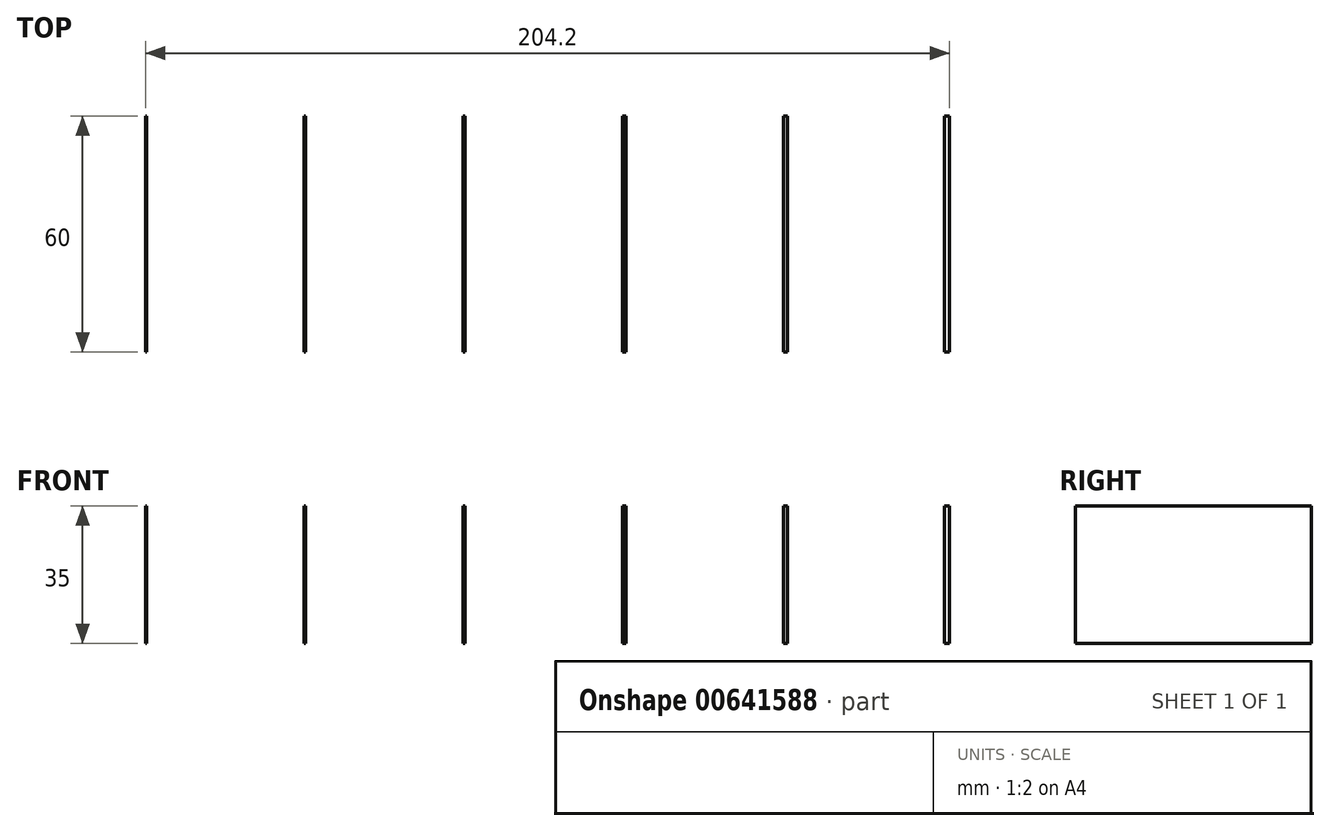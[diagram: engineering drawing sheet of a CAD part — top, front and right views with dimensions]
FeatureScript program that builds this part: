
annotation { "Feature Type Name" : "Feature", "Feature Type Description" : "" }
export const myFeature = defineFeature(function(context is Context, id is Id, definition is map)
    precondition{}
    {
        {
            var Q0;
            Q0=qCreatedBy(makeId("Top.planeOp"),FACE);
            var sketch = newSketch(context, id + "F0", { "sketchPlane" : qUnion([Q0])});
            skLineSegment(sketch, "E0.bottom", {"start": v(-7.2, 180) * mm, "end": v(-6, 180) * mm});
            skLineSegment(sketch, "E0.top", {"start": v(-7.2, 120) * mm, "end": v(-6, 120) * mm});
            skLineSegment(sketch, "E0.left", {"start": v(-7.2, 180) * mm, "end": v(-7.2, 120) * mm});
            skLineSegment(sketch, "E0.right", {"start": v(-6, 180) * mm, "end": v(-6, 120) * mm});
            skLineSegment(sketch, "E1.bottom", {"start": v(-47.2, 120) * mm, "end": v(-48.2, 120) * mm});
            skLineSegment(sketch, "E1.top", {"start": v(-47.2, 180) * mm, "end": v(-48.2, 180) * mm});
            skLineSegment(sketch, "E1.left", {"start": v(-47.2, 120) * mm, "end": v(-47.2, 180) * mm});
            skLineSegment(sketch, "E1.right", {"start": v(-48.2, 120) * mm, "end": v(-48.2, 180) * mm});
            skLineSegment(sketch, "E2.bottom", {"start": v(-88.2, 120) * mm, "end": v(-89, 120) * mm});
            skLineSegment(sketch, "E2.top", {"start": v(-88.2, 180) * mm, "end": v(-89, 180) * mm});
            skLineSegment(sketch, "E2.left", {"start": v(-88.2, 120) * mm, "end": v(-88.2, 180) * mm});
            skLineSegment(sketch, "E2.right", {"start": v(-89, 120) * mm, "end": v(-89, 180) * mm});
            skLineSegment(sketch, "E3.bottom", {"start": v(-129, 120) * mm, "end": v(-129.6, 120) * mm});
            skLineSegment(sketch, "E3.top", {"start": v(-129, 180) * mm, "end": v(-129.6, 180) * mm});
            skLineSegment(sketch, "E3.left", {"start": v(-129, 120) * mm, "end": v(-129, 180) * mm});
            skLineSegment(sketch, "E3.right", {"start": v(-129.6, 120) * mm, "end": v(-129.6, 180) * mm});
            skLineSegment(sketch, "E4.bottom", {"start": v(-169.6, 120) * mm, "end": v(-170, 120) * mm});
            skLineSegment(sketch, "E4.top", {"start": v(-169.6, 180) * mm, "end": v(-170, 180) * mm});
            skLineSegment(sketch, "E4.left", {"start": v(-169.6, 120) * mm, "end": v(-169.6, 180) * mm});
            skLineSegment(sketch, "E4.right", {"start": v(-170, 120) * mm, "end": v(-170, 180) * mm});
            skLineSegment(sketch, "E5.bottom", {"start": v(-210, 120) * mm, "end": v(-210.2, 120) * mm});
            skLineSegment(sketch, "E5.top", {"start": v(-210, 180) * mm, "end": v(-210.2, 180) * mm});
            skLineSegment(sketch, "E5.left", {"start": v(-210, 120) * mm, "end": v(-210, 180) * mm});
            skLineSegment(sketch, "E5.right", {"start": v(-210.2, 120) * mm, "end": v(-210.2, 180) * mm});
            skSolve(sketch);
        }
        {
            var Q0;
            Q0 = qSketchRegion(id + "F0", true);
            extrude(context, id + "F1", {"entities" : qUnion([Q0]), "depth" : 35 * mm, "offsetDistance" : 25 * mm});
        }
    });
